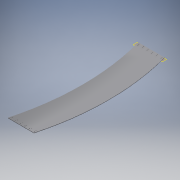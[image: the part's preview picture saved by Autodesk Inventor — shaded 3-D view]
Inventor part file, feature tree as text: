
AUTODESK INVENTOR PART (.ipt)
format: ipt  version: 2016 (Build 200138000, 138)  size: 128,512 bytes
history: native  units: mm
features: reference x28, extrude x2, sketch x2, plane x1
ambient origin geometry x8: Origin, YZ Plane, XZ Plane, XY Plane, X Axis, Y Axis, Z Axis, Center Point
bodies: Solid1 (feature_tree)
feature tree (33):
  plane  "Work Plane1"
  extrude  "Extrusion1"  Depth=5.0mm TaperAngle=0.0deg
  extrude  "Extrusion2"  [1 undecoded]
  sketch  "Sketch1"  dims[d0=5.0mm d1=0.0mm d2=5.0mm d3=0.0mm]
  reference  "Reference1"
  reference  "Reference2"
  reference  "Reference3"
  reference  "Reference4"
  sketch  "Sketch2"
  reference  "Reference5"
  reference  "Reference6"
  reference  "Reference7"
  reference  "Reference8"
  reference  "Reference9"
  reference  "Reference10"
  reference  "Reference11"
  reference  "Reference12"
  reference  "Reference13"
  reference  "Reference14"
  reference  "Reference15"
  reference  "Reference16"
  reference  "Reference17"
  reference  "Reference18"
  reference  "Reference19"
  reference  "Reference20"
  reference  "Reference21"
  reference  "Reference22"
  reference  "Reference23"
  reference  "Reference24"
  reference  "Reference25"
  reference  "Reference26"
  reference  "Reference27"
  reference  "Reference28"
note: 1 required parameter value undecoded (feature->parameter linkage not recoverable at this tier; creation-order binding heuristic only, values carry confidence <= 0.55)
